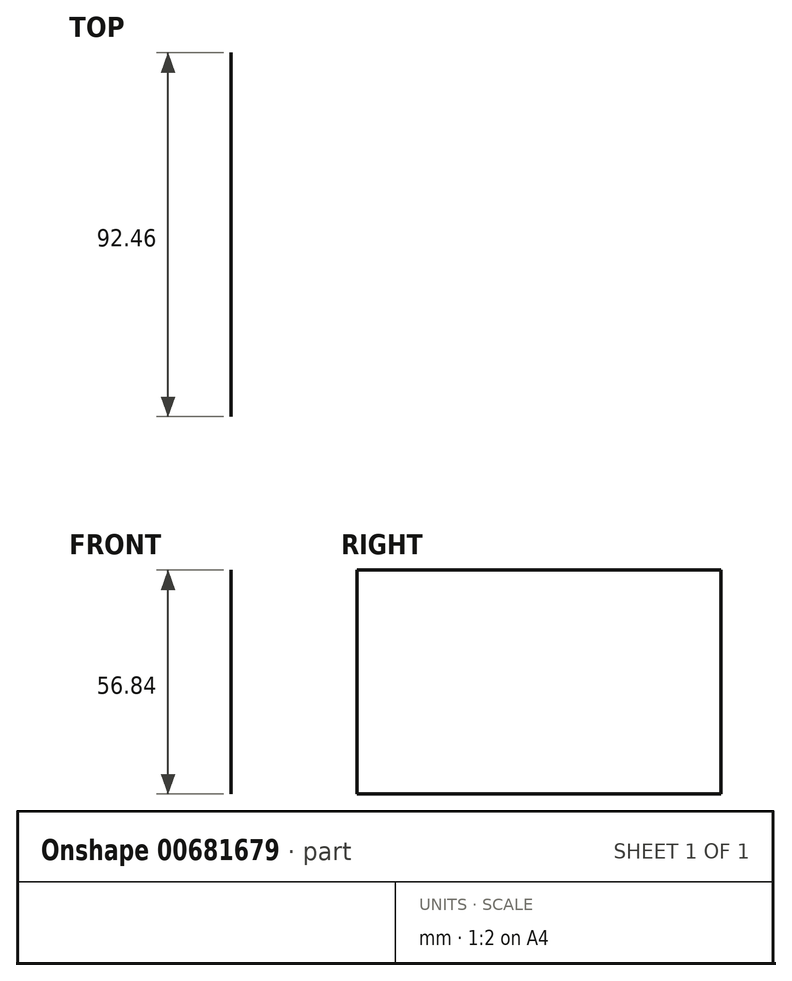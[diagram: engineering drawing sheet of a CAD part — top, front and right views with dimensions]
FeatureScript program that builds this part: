
annotation { "Feature Type Name" : "Feature", "Feature Type Description" : "" }
export const myFeature = defineFeature(function(context is Context, id is Id, definition is map)
    precondition{}
    {
        {
            var Q0;
            Q0=qCreatedBy(makeId("Front.planeOp"),FACE);
            var sketch = newSketch(context, id + "F0", { "sketchPlane" : qUnion([Q0])});
            skLineSegment(sketch, "E0.bottom", {"start": v(-57.77, 23.4) * mm, "end": v(66.77, 23.4) * mm});
            skLineSegment(sketch, "E0.top", {"start": v(-57.77, 19.21) * mm, "end": v(66.77, 19.21) * mm});
            skLineSegment(sketch, "E0.left", {"start": v(-57.77, 23.4) * mm, "end": v(-57.77, 19.21) * mm});
            skLineSegment(sketch, "E0.right", {"start": v(66.77, 23.4) * mm, "end": v(66.77, 19.21) * mm});
            skLineSegment(sketch, "E1.bottom", {"start": v(-57.77, 19.21) * mm, "end": v(-53.3, 19.21) * mm});
            skLineSegment(sketch, "E1.top", {"start": v(-57.77, -39.4) * mm, "end": v(-53.3, -39.4) * mm});
            skLineSegment(sketch, "E1.left", {"start": v(-57.77, 19.21) * mm, "end": v(-57.77, -39.4) * mm});
            skLineSegment(sketch, "E1.right", {"start": v(-53.3, 19.21) * mm, "end": v(-53.3, -39.4) * mm});
            skLineSegment(sketch, "E2.bottom", {"start": v(66.77, 19.21) * mm, "end": v(62.94, 19.21) * mm});
            skLineSegment(sketch, "E2.top", {"start": v(66.77, -37.63) * mm, "end": v(62.94, -37.63) * mm});
            skLineSegment(sketch, "E2.left", {"start": v(66.77, 19.21) * mm, "end": v(66.77, -37.63) * mm});
            skLineSegment(sketch, "E2.right", {"start": v(62.94, 19.21) * mm, "end": v(62.94, -37.63) * mm});
            skLineSegment(sketch, "E3.bottom", {"start": v(-3.78, 19.21) * mm, "end": v(0, 19.21) * mm});
            skLineSegment(sketch, "E3.top", {"start": v(-3.78, -36.4) * mm, "end": v(0, -36.4) * mm});
            skLineSegment(sketch, "E3.left", {"start": v(-3.78, 19.21) * mm, "end": v(-3.78, -36.4) * mm});
            skLineSegment(sketch, "E3.right", {"start": v(0, 19.21) * mm, "end": v(0, -36.4) * mm});
            skSolve(sketch);
        }
        {
            var Q0;
            Q0=sQuery(id+"F0.wireOp",EDGE,"E2.left");
            extrude(context, id + "F1", {"bodyType" : ToolBodyType.SURFACE, "surfaceEntities" : qUnion([Q0]), "depth" : 92.46 * mm, "offsetDistance" : 25.4 * mm});
        }
    });
